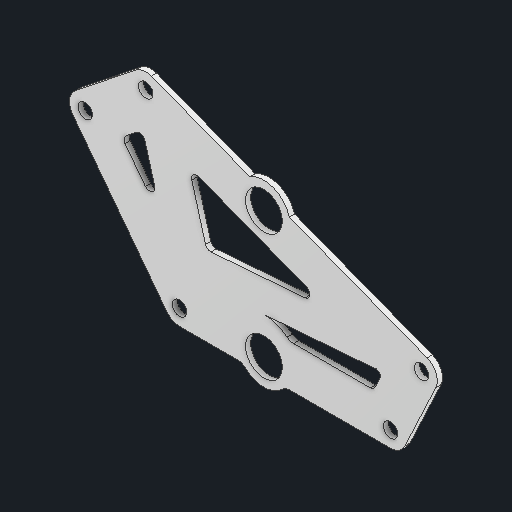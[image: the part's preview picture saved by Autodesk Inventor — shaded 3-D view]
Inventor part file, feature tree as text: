
AUTODESK INVENTOR PART (.ipt)
format: ipt  version: 2025 (Build 290162000, 162)  size: 179,200 bytes
history: native  units: in
note: dims shown in document units (in); Inventor stores cm internally (conversion verified against a paired STEP export)
features: other x5, sketch x1
ambient origin geometry x8: Origin, YZ Plane, XZ Plane, XY Plane, X Axis, Y Axis, Z Axis, Center Point
bodies: Solid1 (feature_tree)
feature tree (6):
  other  "gearbox_gusset.ipt"
  other  "Blocks"
  other  "main"
  other  "Solid1::gearbox_gusset.ipt"
  other  "TaggingFeature1"
  sketch  "Sketch1"  dims[d0=0.3937in]
